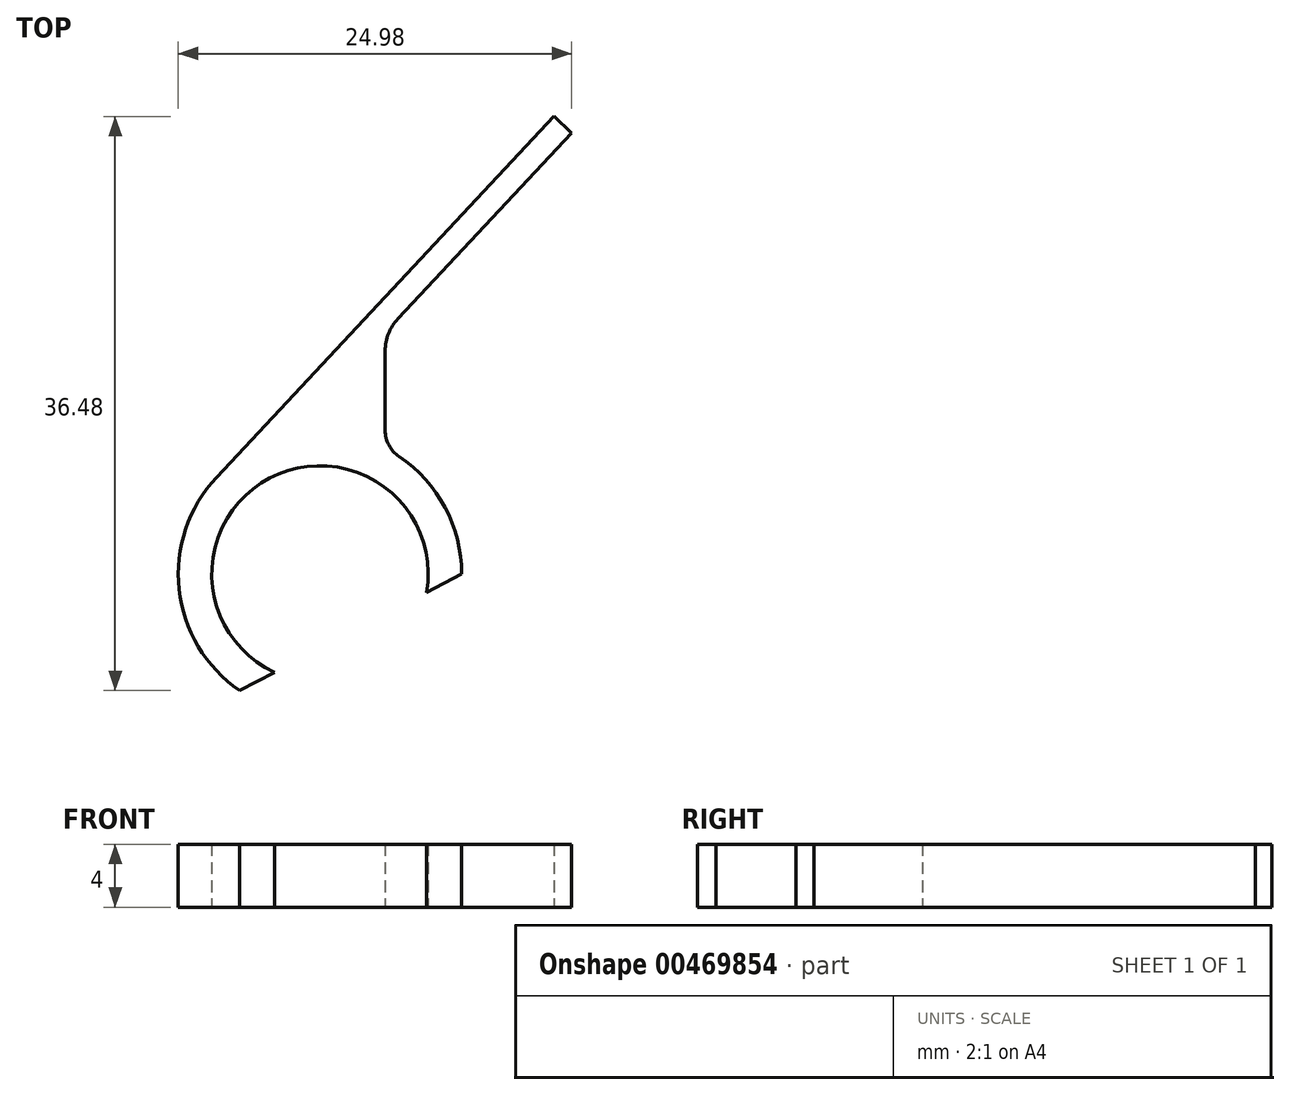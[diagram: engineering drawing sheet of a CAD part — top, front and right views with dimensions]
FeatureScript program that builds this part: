
annotation { "Feature Type Name" : "Feature", "Feature Type Description" : "" }
export const myFeature = defineFeature(function(context is Context, id is Id, definition is map)
    precondition{}
    {
        {
            var Q0;
            Q0=qCreatedBy(makeId("Top.planeOp"),FACE);
            var sketch = newSketch(context, id + "F0", { "sketchPlane" : qUnion([Q0])});
            skArc(sketch, "E0", {"start": v(-6.57, 6.15) * mm, "mid": v(1.02, -8.94) * mm, "end": v(5.02, 7.47) * mm});
            skLineSegment(sketch, "E1", {"start": v(-6.57, 6.15) * mm, "end": v(14.86, 29.07) * mm});
            skLineSegment(sketch, "E2", {"start": v(4.95, 16.22) * mm, "end": v(15.98, 28.02) * mm});
            skLineSegment(sketch, "E3", {"start": v(14.86, 29.07) * mm, "end": v(15.98, 28.02) * mm});
            skLineSegment(sketch, "E4", {"start": v(4.14, 9.13) * mm, "end": v(4.14, 14.17) * mm});
            skPoint(sketch, "E5.visualSharp", {"position": v(4.14, 15.36) * mm});
            skArc(sketch, "E5.filletArc", {"start": v(4.95, 16.22) * mm, "mid": v(4.35, 15.27) * mm, "end": v(4.14, 14.17) * mm});
            skPoint(sketch, "E6.visualSharp", {"position": v(4.14, 8) * mm});
            skArc(sketch, "E6.filletArc", {"start": v(4.14, 9.13) * mm, "mid": v(4.37, 8.19) * mm, "end": v(5.02, 7.47) * mm});
            skCircle(sketch, "E7", {"center": v(0, 0) * mm, "radius": 6.88 * mm});
            skSolve(sketch);
        }
        {
            var Q0;
            Q0=makeQuery(id+"F0.imprint","IMPRINT",FACE,{"disambiguationData":[TD([[makeQuery(id+"F0.imprint","IMPRINT",EDGE,{"derivedFrom":sQuery(id+"F0.wireOp",EDGE,"E0")}),1.0]])]});
            extrude(context, id + "F1", {"entities" : qUnion([Q0]), "depth" : 4 * mm});
        }
        {
            var Q0;
            Q0=makeQuery(id+"F1.opExtrude","CAP_FACE",FACE,{"disambiguationData":[OSD([sQuery(id+"F0.wireOp",EDGE,"E0"),sQuery(id+"F0.wireOp",EDGE,"E1"),sQuery(id+"F0.wireOp",EDGE,"E2"),sQuery(id+"F0.wireOp",EDGE,"E3"),sQuery(id+"F0.wireOp",EDGE,"E4"),sQuery(id+"F0.wireOp",EDGE,"E5.filletArc"),sQuery(id+"F0.wireOp",EDGE,"E6.filletArc"),sQuery(id+"F0.wireOp",EDGE,"E7")])],"isStart":false});
            var sketch = newSketch(context, id + "F2", { "sketchPlane" : qUnion([Q0])});
            skLineSegment(sketch, "E8", {"start": v(-5.11, -7.4) * mm, "end": v(9, 0) * mm});
            skLineSegment(sketch, "E9", {"start": v(-5.11, -7.4) * mm, "end": v(-2.87, -11.67) * mm});
            skLineSegment(sketch, "E10", {"start": v(-2.87, -11.67) * mm, "end": v(10.05, -4.89) * mm});
            skLineSegment(sketch, "E11", {"start": v(10.05, -4.89) * mm, "end": v(9, 0) * mm});
            skSolve(sketch);
        }
        {
            var Q0;
            {var subQ0=sQuery(id+"F2.wireOp",EDGE,"E9");Q0=makeQuery(id+"F2.imprint","IMPRINT",FACE,{"disambiguationData":[TD([[makeQuery(id+"F2.imprint","IMPRINT",EDGE,{"derivedFrom":subQ0}),1.0]])]});}
            var Q1;
            {var subQ0=sQuery(id+"F2.wireOp",EDGE,"E8");var subQ3=makeQuery(id+"F1.opExtrude","CAP_EDGE",EDGE,{"disambiguationData":[OSD([sQuery(id+"F0.wireOp",EDGE,"E7")])],"isStart":false});var subQ4=makeQuery(id+"F2.imprint","INTERSECT",VERTEX,{"disambiguationData":[OD(0.0)],"derivedFrom":[subQ3,subQ0]});Q1=makeQuery(id+"F2.imprint","IMPRINT",FACE,{"disambiguationData":[TD([[makeQuery(id+"F2.imprint","IMPRINT",EDGE,{"disambiguationData":[TD([[subQ4,-1.0]])],"derivedFrom":subQ3}),-1.0]])]});}
            var Q2;
            {var subQ0=sQuery(id+"F2.wireOp",EDGE,"E8");var subQ1=makeQuery(id+"F1.opExtrude","CAP_EDGE",EDGE,{"disambiguationData":[OSD([sQuery(id+"F0.wireOp",EDGE,"E7")])],"isStart":false});var subQ2=makeQuery(id+"F2.imprint","INTERSECT",VERTEX,{"disambiguationData":[OD(0.0)],"derivedFrom":[subQ1,subQ0]});Q2=makeQuery(id+"F2.imprint","IMPRINT",FACE,{"disambiguationData":[TD([[makeQuery(id+"F2.imprint","IMPRINT",EDGE,{"disambiguationData":[TD([[subQ2,-1.0]])],"derivedFrom":subQ0}),-1.0]])]});}
            extrude(context, id + "F3", {"entities" : qUnion([Q0, Q1, Q2]), "operationType" : NewBodyOperationType.REMOVE, "endBound" : BoundingType.THROUGH_ALL, "oppositeDirection" : true, "depth" : 25 * mm});
        }
    });
